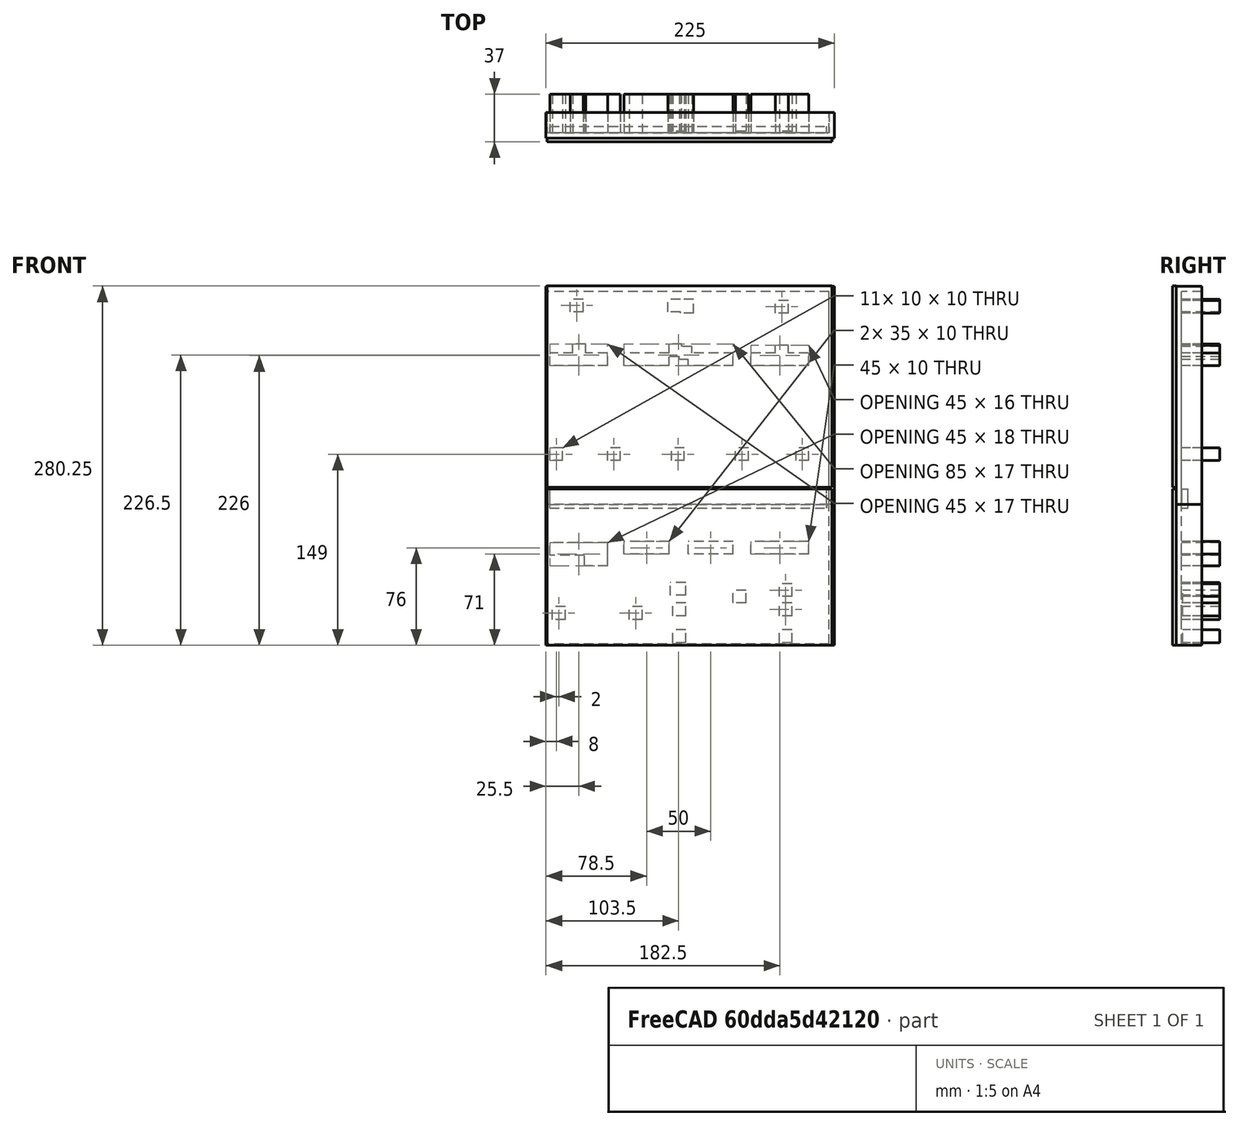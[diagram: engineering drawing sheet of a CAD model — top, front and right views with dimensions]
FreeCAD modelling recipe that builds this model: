
FCSTD DOCUMENT  (FreeCAD 0.19R24291 (Git))
Label: estructuraBase
License: All rights reserved
LicenseURL: http://en.wikipedia.org/wiki/All_rights_reserved
objects: Part::Box×154, Part::MultiFuse×11, Part::Cut×7, Part::Feature×2
note: 174 computed .brp shape members not serialized (recipe doc carries the construction recipe); baked Part::Feature solids carry a one-line shape summary decoded from their .brp

FEATURE [Part::Box] Box  label="Cubo"
  AttacherType = Attacher::AttachEngine3D
  Height = 275
  Length = 220
  Placement = pos=(-171,-24,-147) rot=(0,0,1;0rad)
  Width = 4
FEATURE [Part::Box] Box001  label="Cubo001"
  AttacherType = Attacher::AttachEngine3D
  Height = 10
  Length = 35
  Placement = pos=(-96,-54,70) rot=(0,0,1;0rad)
  Width = 30
FEATURE [Part::Box] Box002  label="Cubo002"
  AttacherType = Attacher::AttachEngine3D
  Height = 10
  Length = 10
  Placement = pos=(-142,-54,-110) rot=(0,0,1;0rad)
  Width = 30
FEATURE [Part::Box] Box004  label="Cubo004"
  AttacherType = Attacher::AttachEngine3D
  Height = 10
  Length = 10
  Placement = pos=(-142,-54,-125) rot=(0,0,1;0rad)
  Width = 30
FEATURE [Part::Box] Box005  label="Cubo005"
  AttacherType = Attacher::AttachEngine3D
  Height = 10
  Length = 10
  Placement = pos=(-106,-54,-115) rot=(0,0,1;0rad)
  Width = 28.9
FEATURE [Part::Box] Box006  label="Cubo006"
  AttacherType = Attacher::AttachEngine3D
  Height = 10
  Length = 10
  Placement = pos=(-142,-54,-146) rot=(0,0,1;0rad)
  Width = 28.9
FEATURE [Part::Box] Box007  label="Cubo007"
  AttacherType = Attacher::AttachEngine3D
  Height = 10
  Length = 10
  Placement = pos=(-59,-54,-146) rot=(0,0,1;0rad)
  Width = 28.9
FEATURE [Part::Box] Box008  label="Cubo008"
  AttacherType = Attacher::AttachEngine3D
  Height = 10
  Length = 10
  Placement = pos=(-59,-54,-125) rot=(0,0,1;0rad)
  Width = 28.9
FEATURE [Part::Box] Box009  label="Cubo009"
  AttacherType = Attacher::AttachEngine3D
  Height = 10
  Length = 12
  Placement = pos=(-59,-54,-109) rot=(0,0,1;0rad)
  Width = 30
FEATURE [Part::Box] Box010  label="Cubo010"
  AttacherType = Attacher::AttachEngine3D
  Height = 10
  Length = 45
  Placement = pos=(-155,-54,70) rot=(0,0,1;0rad)
  Width = 30
FEATURE [Part::Box] Box011  label="Cubo011"
  AttacherType = Attacher::AttachEngine3D
  Height = 10
  Length = 35
  Placement = pos=(-46,-54,70) rot=(0,0,1;0rad)
  Width = 30
FEATURE [Part::Box] Box012  label="Cubo012"
  AttacherType = Attacher::AttachEngine3D
  Height = 10
  Length = 45
  Placement = pos=(2,-54,70) rot=(0,0,1;0rad)
  Width = 30
FEATURE [Part::Box] Box013  label="Cubo013"
  AttacherType = Attacher::AttachEngine3D
  Height = 10
  Length = 35
  Placement = pos=(-96,-54,-77) rot=(0,0,1;0rad)
  Width = 30
FEATURE [Part::Box] Box014  label="Cubo014"
  AttacherType = Attacher::AttachEngine3D
  Height = 10
  Length = 45
  Placement = pos=(-155,-54,-77) rot=(0,0,1;0rad)
  Width = 30
FEATURE [Part::Box] Box015  label="Cubo015"
  AttacherType = Attacher::AttachEngine3D
  Height = 10
  Length = 35
  Placement = pos=(-46,-54,-77) rot=(0,0,1;0rad)
  Width = 30
FEATURE [Part::Box] Box016  label="Cubo016"
  AttacherType = Attacher::AttachEngine3D
  Height = 10
  Length = 45
  Placement = pos=(2,-54,-78) rot=(0,0,1;0rad)
  Width = 30
FEATURE [Part::Box] Box017  label="Cubo017"
  AttacherType = Attacher::AttachEngine3D
  Height = 10
  Length = 10
  Placement = pos=(-25,-54,-128) rot=(0,0,1;0rad)
  Width = 30
FEATURE [Part::Box] Box018  label="Cubo018"
  AttacherType = Attacher::AttachEngine3D
  Height = 10
  Length = 10
  Placement = pos=(35,-54,-128) rot=(0,0,1;0rad)
  Width = 30
FEATURE [Part::Box] Box019  label="Cubo019"
  AttacherType = Attacher::AttachEngine3D
  Height = 10
  Length = 18
  Placement = pos=(2,-54,-86) rot=(0,0,1;0rad)
  Width = 30
FEATURE [Part::Box] Box020  label="Cubo020"
  AttacherType = Attacher::AttachEngine3D
  Height = 10
  Length = 10
  Placement = pos=(-56,-54,77) rot=(0,0,1;0rad)
  Width = 30
FEATURE [Part::Box] Box021  label="Cubo021"
  AttacherType = Attacher::AttachEngine3D
  Height = 10
  Length = 10
  Placement = pos=(21,-54,112) rot=(0,0,1;0rad)
  Width = 30
FEATURE [Part::Box] Box022  label="Cubo022"
  AttacherType = Attacher::AttachEngine3D
  Height = 10
  Length = 10
  Placement = pos=(-55,-54,112) rot=(0,0,1;0rad)
  Width = 30
FEATURE [Part::Box] Box023  label="Cubo023"
  AttacherType = Attacher::AttachEngine3D
  Height = 10
  Length = 10
  Placement = pos=(19,-54,77) rot=(0,0,1;0rad)
  Width = 30
FEATURE [Part::Box] Box024  label="Cubo024"
  AttacherType = Attacher::AttachEngine3D
  Height = 11
  Length = 10
  Placement = pos=(-65,-54,111) rot=(0,0,1;0rad)
  Width = 30
FEATURE [Part::Box] Box025  label="Cubo025"
  AttacherType = Attacher::AttachEngine3D
  Height = 10
  Length = 10
  Placement = pos=(-139,-54,111) rot=(0,0,1;0rad)
  Width = 30
FEATURE [Part::Box] Box026  label="Cubo026"
  AttacherType = Attacher::AttachEngine3D
  Height = 10
  Length = 10
  Placement = pos=(-139,-54,76) rot=(0,0,1;0rad)
  Width = 30
FEATURE [Part::Box] Box027  label="Cubo027"
  AttacherType = Attacher::AttachEngine3D
  Height = 10
  Length = 10
  Placement = pos=(-64,-54,75) rot=(0,0,1;0rad)
  Width = 30
FEATURE [Part::Box] Box028  label="Cubo028"
  AttacherType = Attacher::AttachEngine3D
  Height = 10
  Length = 10
  Placement = pos=(-155,-54,-4) rot=(0,0,1;0rad)
  Width = 30
FEATURE [Part::Box] Box029  label="Cubo029"
  AttacherType = Attacher::AttachEngine3D
  Height = 10
  Length = 10
  Placement = pos=(37,-54,-4) rot=(0,0,1;0rad)
  Width = 30
FEATURE [Part::Box] Box030  label="Cubo030"
  AttacherType = Attacher::AttachEngine3D
  Height = 10
  Length = 10
  Placement = pos=(-108,-54,-4) rot=(0,0,1;0rad)
  Width = 30
FEATURE [Part::Box] Box031  label="Cubo031"
  AttacherType = Attacher::AttachEngine3D
  Height = 10
  Length = 10
  Placement = pos=(-58,-54,-4) rot=(0,0,1;0rad)
  Width = 30
FEATURE [Part::Box] Box032  label="Cubo032"
  AttacherType = Attacher::AttachEngine3D
  Height = 10
  Length = 10
  Placement = pos=(-8,-54,-4) rot=(0,0,1;0rad)
  Width = 30
FEATURE [Part::Box] Box033  label="Cubo033"
  AttacherType = Attacher::AttachEngine3D
  Height = 275
  Length = 1
  Placement = pos=(-49,40,-147) rot=(0,0,1;3.14159rad)
  Width = 20
FEATURE [Part::Box] Box034  label="Cubo034"
  AttacherType = Attacher::AttachEngine3D
  Height = 275
  Length = 4
  Placement = pos=(175,40,-147) rot=(0,0,1;3.14159rad)
  Width = 20
FEATURE [Part::Box] Box035  label="Cubo035"
  AttacherType = Attacher::AttachEngine3D
  Height = 4
  Length = 225
  Placement = pos=(175,40,128) rot=(0,0,1;3.14159rad)
  Width = 20
FEATURE [Part::Box] Box036  label="Cubo036"
  AttacherType = Attacher::AttachEngine3D
  Height = 1
  Length = 225
  Placement = pos=(175,40,-148) rot=(0,0,1;3.14159rad)
  Width = 20
FEATURE [Part::Box] Box037  label="Cubo037"
  AttacherType = Attacher::AttachEngine3D
  Height = 200
  Length = 300
  Placement = pos=(-111,11,-38) rot=(0,0,1;0rad)
  Width = 50
FEATURE [Part::Feature] Cut002_solid  label="Parte1 (Solid)001"
  shape: bbox 222 x 37 x 122 mm, 103 faces (baked)
FEATURE [Part::Box] Box039  label="Cubo039"
  AttacherType = Attacher::AttachEngine3D
  Height = 157
  Length = 222
  Placement = pos=(-49,17,-24.75) rot=(0,0,1;0rad)
  Width = 3
FEATURE [Part::Box] Box041  label="Cubo041"
  AttacherType = Attacher::AttachEngine3D
  Height = 107
  Length = 222
  Placement = pos=(-49,17,-148) rot=(0,0,1;0rad)
  Width = 3
FEATURE [Part::Box] Box042  label="Cubo042"
  AttacherType = Attacher::AttachEngine3D
  Height = 15
  Length = 2
  Placement = pos=(-49,17,-41) rot=(0,0,1;0rad)
  Width = 3
FEATURE [Part::Box] Box043  label="Cubo043"
  AttacherType = Attacher::AttachEngine3D
  Height = 15
  Length = 4
  Placement = pos=(169,17,-41) rot=(0,0,1;0rad)
  Width = 3
FEATURE [Part::Box] Box044  label="Cubo044"
  AttacherType = Attacher::AttachEngine3D
  Height = 12
  Length = 222
  Placement = pos=(-49,24,-38) rot=(0,0,1;0rad)
  Width = 0.25
FEATURE [Part::MultiFuse] Fusion
  Placement = pos=(0,0,0) rot=(0,0,1;3.14159rad)
  Shapes = -> [Box,Box001,Box002,Box004,Box005,Box006,Box007,Box009,Box008,Box010,Box012,Box011,Box013,Box014,Box015,Box016,Box018,Box017,Box019,Box020,Box021,Box022,Box023,Box032,Box031,Box030,Box028,Box027,Box024,Box025,Box026,Box029]
FEATURE [Part::MultiFuse] Fusion010  label="CompletoConParedes"
  Shapes = -> [Fusion,Box033,Box034,Box035,Box036]
FEATURE [Part::Box] Box045  label="Cubo045"
  AttacherType = Attacher::AttachEngine3D
  Height = 275
  Length = 220
  Placement = pos=(-171,-24,-147) rot=(0,0,1;0rad)
  Width = 4
FEATURE [Part::Box] Box046  label="Cubo046"
  AttacherType = Attacher::AttachEngine3D
  Height = 10
  Length = 35
  Placement = pos=(-96,-54,70) rot=(0,0,1;0rad)
  Width = 30
FEATURE [Part::Box] Box047  label="Cubo047"
  AttacherType = Attacher::AttachEngine3D
  Height = 10
  Length = 10
  Placement = pos=(-142,-54,-110) rot=(0,0,1;0rad)
  Width = 30
FEATURE [Part::Box] Box048  label="Cubo048"
  AttacherType = Attacher::AttachEngine3D
  Height = 10
  Length = 10
  Placement = pos=(-142,-54,-125) rot=(0,0,1;0rad)
  Width = 30
FEATURE [Part::Box] Box049  label="Cubo049"
  AttacherType = Attacher::AttachEngine3D
  Height = 10
  Length = 10
  Placement = pos=(-106,-54,-115) rot=(0,0,1;0rad)
  Width = 28.9
FEATURE [Part::Box] Box050  label="Cubo050"
  AttacherType = Attacher::AttachEngine3D
  Height = 10
  Length = 10
  Placement = pos=(-142,-54,-146) rot=(0,0,1;0rad)
  Width = 28.9
FEATURE [Part::Box] Box051  label="Cubo051"
  AttacherType = Attacher::AttachEngine3D
  Height = 10
  Length = 10
  Placement = pos=(-59,-54,-146) rot=(0,0,1;0rad)
  Width = 28.9
FEATURE [Part::Box] Box052  label="Cubo052"
  AttacherType = Attacher::AttachEngine3D
  Height = 10
  Length = 10
  Placement = pos=(-59,-54,-125) rot=(0,0,1;0rad)
  Width = 28.9
FEATURE [Part::Box] Box053  label="Cubo053"
  AttacherType = Attacher::AttachEngine3D
  Height = 10
  Length = 12
  Placement = pos=(-59,-54,-109) rot=(0,0,1;0rad)
  Width = 30
FEATURE [Part::Box] Box054  label="Cubo054"
  AttacherType = Attacher::AttachEngine3D
  Height = 10
  Length = 45
  Placement = pos=(-155,-54,70) rot=(0,0,1;0rad)
  Width = 30
FEATURE [Part::Box] Box055  label="Cubo055"
  AttacherType = Attacher::AttachEngine3D
  Height = 10
  Length = 35
  Placement = pos=(-46,-54,70) rot=(0,0,1;0rad)
  Width = 30
FEATURE [Part::Box] Box056  label="Cubo056"
  AttacherType = Attacher::AttachEngine3D
  Height = 10
  Length = 45
  Placement = pos=(2,-54,70) rot=(0,0,1;0rad)
  Width = 30
FEATURE [Part::Box] Box057  label="Cubo057"
  AttacherType = Attacher::AttachEngine3D
  Height = 10
  Length = 35
  Placement = pos=(-96,-54,-77) rot=(0,0,1;0rad)
  Width = 30
FEATURE [Part::Box] Box058  label="Cubo058"
  AttacherType = Attacher::AttachEngine3D
  Height = 10
  Length = 45
  Placement = pos=(-155,-54,-77) rot=(0,0,1;0rad)
  Width = 30
FEATURE [Part::Box] Box059  label="Cubo059"
  AttacherType = Attacher::AttachEngine3D
  Height = 10
  Length = 35
  Placement = pos=(-46,-54,-77) rot=(0,0,1;0rad)
  Width = 30
FEATURE [Part::Box] Box060  label="Cubo060"
  AttacherType = Attacher::AttachEngine3D
  Height = 10
  Length = 45
  Placement = pos=(2,-54,-78) rot=(0,0,1;0rad)
  Width = 30
FEATURE [Part::Box] Box061  label="Cubo061"
  AttacherType = Attacher::AttachEngine3D
  Height = 10
  Length = 10
  Placement = pos=(-25,-54,-128) rot=(0,0,1;0rad)
  Width = 30
FEATURE [Part::Box] Box062  label="Cubo062"
  AttacherType = Attacher::AttachEngine3D
  Height = 10
  Length = 10
  Placement = pos=(35,-54,-128) rot=(0,0,1;0rad)
  Width = 30
FEATURE [Part::Box] Box063  label="Cubo063"
  AttacherType = Attacher::AttachEngine3D
  Height = 10
  Length = 18
  Placement = pos=(2,-54,-86) rot=(0,0,1;0rad)
  Width = 30
FEATURE [Part::Box] Box064  label="Cubo064"
  AttacherType = Attacher::AttachEngine3D
  Height = 10
  Length = 10
  Placement = pos=(-56,-54,77) rot=(0,0,1;0rad)
  Width = 30
FEATURE [Part::Box] Box065  label="Cubo065"
  AttacherType = Attacher::AttachEngine3D
  Height = 10
  Length = 10
  Placement = pos=(21,-54,112) rot=(0,0,1;0rad)
  Width = 30
FEATURE [Part::Box] Box066  label="Cubo066"
  AttacherType = Attacher::AttachEngine3D
  Height = 10
  Length = 10
  Placement = pos=(-55,-54,112) rot=(0,0,1;0rad)
  Width = 30
FEATURE [Part::Box] Box067  label="Cubo067"
  AttacherType = Attacher::AttachEngine3D
  Height = 10
  Length = 10
  Placement = pos=(19,-54,77) rot=(0,0,1;0rad)
  Width = 30
FEATURE [Part::Box] Box068  label="Cubo068"
  AttacherType = Attacher::AttachEngine3D
  Height = 11
  Length = 10
  Placement = pos=(-65,-54,111) rot=(0,0,1;0rad)
  Width = 30
FEATURE [Part::Box] Box069  label="Cubo069"
  AttacherType = Attacher::AttachEngine3D
  Height = 10
  Length = 10
  Placement = pos=(-139,-54,111) rot=(0,0,1;0rad)
  Width = 30
FEATURE [Part::Box] Box070  label="Cubo070"
  AttacherType = Attacher::AttachEngine3D
  Height = 10
  Length = 10
  Placement = pos=(-139,-54,76) rot=(0,0,1;0rad)
  Width = 30
FEATURE [Part::Box] Box071  label="Cubo071"
  AttacherType = Attacher::AttachEngine3D
  Height = 10
  Length = 10
  Placement = pos=(-64,-54,75) rot=(0,0,1;0rad)
  Width = 30
FEATURE [Part::Box] Box072  label="Cubo072"
  AttacherType = Attacher::AttachEngine3D
  Height = 10
  Length = 10
  Placement = pos=(-155,-54,-4) rot=(0,0,1;0rad)
  Width = 30
FEATURE [Part::Box] Box073  label="Cubo073"
  AttacherType = Attacher::AttachEngine3D
  Height = 10
  Length = 10
  Placement = pos=(37,-54,-4) rot=(0,0,1;0rad)
  Width = 30
FEATURE [Part::Box] Box074  label="Cubo074"
  AttacherType = Attacher::AttachEngine3D
  Height = 10
  Length = 10
  Placement = pos=(-108,-54,-4) rot=(0,0,1;0rad)
  Width = 30
FEATURE [Part::Box] Box075  label="Cubo075"
  AttacherType = Attacher::AttachEngine3D
  Height = 10
  Length = 10
  Placement = pos=(-58,-54,-4) rot=(0,0,1;0rad)
  Width = 30
FEATURE [Part::Box] Box076  label="Cubo076"
  AttacherType = Attacher::AttachEngine3D
  Height = 10
  Length = 10
  Placement = pos=(-8,-54,-4) rot=(0,0,1;0rad)
  Width = 30
FEATURE [Part::Box] Box077  label="Cubo077"
  AttacherType = Attacher::AttachEngine3D
  Height = 275
  Length = 1
  Placement = pos=(-49,40,-147) rot=(0,0,1;3.14159rad)
  Width = 20
FEATURE [Part::Box] Box078  label="Cubo078"
  AttacherType = Attacher::AttachEngine3D
  Height = 275
  Length = 4
  Placement = pos=(175,40,-147) rot=(0,0,1;3.14159rad)
  Width = 20
FEATURE [Part::Box] Box079  label="Cubo079"
  AttacherType = Attacher::AttachEngine3D
  Height = 4
  Length = 225
  Placement = pos=(175,40,128) rot=(0,0,1;3.14159rad)
  Width = 20
FEATURE [Part::Box] Box080  label="Cubo080"
  AttacherType = Attacher::AttachEngine3D
  Height = 1
  Length = 225
  Placement = pos=(175,40,-148) rot=(0,0,1;3.14159rad)
  Width = 20
FEATURE [Part::MultiFuse] Fusion011
  Placement = pos=(0,0,0) rot=(0,0,1;3.14159rad)
  Shapes = -> [Box045,Box046,Box047,Box048,Box049,Box050,Box051,Box053,Box052,Box054,Box056,Box055,Box057,Box058,Box059,Box060,Box062,Box061,Box063,Box064,Box065,Box066,Box067,Box076,Box075,Box074,Box072,Box071,Box068,Box069,Box070,Box073]
FEATURE [Part::MultiFuse] Fusion012  label="CompletoConParedes001"
  Shapes = -> [Fusion011,Box077,Box078,Box079,Box080]
FEATURE [Part::Cut] Cut
  Base = -> Fusion012
  Tool = -> Box037
FEATURE [Part::Box] Box081  label="Cubo081"
  AttacherType = Attacher::AttachEngine3D
  Height = 200
  Length = 300
  Placement = pos=(-111,11,-38) rot=(0,0,1;0rad)
  Width = 50
FEATURE [Part::Box] Box082  label="Cubo082"
  AttacherType = Attacher::AttachEngine3D
  Height = 10
  Length = 10
  Placement = pos=(35,-54,-128) rot=(0,0,1;0rad)
  Width = 30
FEATURE [Part::Box] Box083  label="Cubo083"
  AttacherType = Attacher::AttachEngine3D
  Height = 10
  Length = 18
  Placement = pos=(2,-54,-86) rot=(0,0,1;0rad)
  Width = 30
FEATURE [Part::Box] Box084  label="Cubo084"
  AttacherType = Attacher::AttachEngine3D
  Height = 10
  Length = 10
  Placement = pos=(-56,-54,77) rot=(0,0,1;0rad)
  Width = 30
FEATURE [Part::Box] Box085  label="Cubo085"
  AttacherType = Attacher::AttachEngine3D
  Height = 10
  Length = 10
  Placement = pos=(21,-54,112) rot=(0,0,1;0rad)
  Width = 30
FEATURE [Part::Box] Box086  label="Cubo086"
  AttacherType = Attacher::AttachEngine3D
  Height = 10
  Length = 10
  Placement = pos=(-55,-54,112) rot=(0,0,1;0rad)
  Width = 30
FEATURE [Part::Box] Box087  label="Cubo087"
  AttacherType = Attacher::AttachEngine3D
  Height = 10
  Length = 10
  Placement = pos=(19,-54,77) rot=(0,0,1;0rad)
  Width = 30
FEATURE [Part::Box] Box088  label="Cubo088"
  AttacherType = Attacher::AttachEngine3D
  Height = 11
  Length = 10
  Placement = pos=(-65,-54,111) rot=(0,0,1;0rad)
  Width = 30
FEATURE [Part::Box] Box089  label="Cubo089"
  AttacherType = Attacher::AttachEngine3D
  Height = 10
  Length = 10
  Placement = pos=(-139,-54,111) rot=(0,0,1;0rad)
  Width = 30
FEATURE [Part::Box] Box090  label="Cubo090"
  AttacherType = Attacher::AttachEngine3D
  Height = 10
  Length = 10
  Placement = pos=(-139,-54,76) rot=(0,0,1;0rad)
  Width = 30
FEATURE [Part::Box] Box091  label="Cubo091"
  AttacherType = Attacher::AttachEngine3D
  Height = 10
  Length = 10
  Placement = pos=(-142,-54,-146) rot=(0,0,1;0rad)
  Width = 28.9
FEATURE [Part::Box] Box092  label="Cubo092"
  AttacherType = Attacher::AttachEngine3D
  Height = 10
  Length = 10
  Placement = pos=(-59,-54,-146) rot=(0,0,1;0rad)
  Width = 28.9
FEATURE [Part::Box] Box093  label="Cubo093"
  AttacherType = Attacher::AttachEngine3D
  Height = 10
  Length = 10
  Placement = pos=(-59,-54,-125) rot=(0,0,1;0rad)
  Width = 28.9
FEATURE [Part::Box] Box094  label="Cubo094"
  AttacherType = Attacher::AttachEngine3D
  Height = 10
  Length = 12
  Placement = pos=(-59,-54,-109) rot=(0,0,1;0rad)
  Width = 30
FEATURE [Part::Box] Box095  label="Cubo095"
  AttacherType = Attacher::AttachEngine3D
  Height = 10
  Length = 45
  Placement = pos=(-155,-54,70) rot=(0,0,1;0rad)
  Width = 30
FEATURE [Part::Box] Box096  label="Cubo096"
  AttacherType = Attacher::AttachEngine3D
  Height = 10
  Length = 35
  Placement = pos=(-46,-54,70) rot=(0,0,1;0rad)
  Width = 30
FEATURE [Part::Box] Box097  label="Cubo097"
  AttacherType = Attacher::AttachEngine3D
  Height = 10
  Length = 45
  Placement = pos=(2,-54,70) rot=(0,0,1;0rad)
  Width = 30
FEATURE [Part::Box] Box098  label="Cubo098"
  AttacherType = Attacher::AttachEngine3D
  Height = 10
  Length = 35
  Placement = pos=(-96,-54,-77) rot=(0,0,1;0rad)
  Width = 30
FEATURE [Part::Box] Box099  label="Cubo099"
  AttacherType = Attacher::AttachEngine3D
  Height = 10
  Length = 45
  Placement = pos=(-155,-54,-77) rot=(0,0,1;0rad)
  Width = 30
FEATURE [Part::Box] Box100  label="Cubo100"
  AttacherType = Attacher::AttachEngine3D
  Height = 10
  Length = 35
  Placement = pos=(-46,-54,-77) rot=(0,0,1;0rad)
  Width = 30
FEATURE [Part::Box] Box101  label="Cubo101"
  AttacherType = Attacher::AttachEngine3D
  Height = 10
  Length = 45
  Placement = pos=(2,-54,-78) rot=(0,0,1;0rad)
  Width = 30
FEATURE [Part::Box] Box102  label="Cubo102"
  AttacherType = Attacher::AttachEngine3D
  Height = 10
  Length = 10
  Placement = pos=(-25,-54,-128) rot=(0,0,1;0rad)
  Width = 30
FEATURE [Part::Box] Box103  label="Cubo103"
  AttacherType = Attacher::AttachEngine3D
  Height = 10
  Length = 35
  Placement = pos=(-96,-54,70) rot=(0,0,1;0rad)
  Width = 30
FEATURE [Part::Box] Box104  label="Cubo104"
  AttacherType = Attacher::AttachEngine3D
  Height = 10
  Length = 10
  Placement = pos=(-142,-54,-110) rot=(0,0,1;0rad)
  Width = 30
FEATURE [Part::Box] Box105  label="Cubo105"
  AttacherType = Attacher::AttachEngine3D
  Height = 10
  Length = 10
  Placement = pos=(-142,-54,-125) rot=(0,0,1;0rad)
  Width = 30
FEATURE [Part::Box] Box106  label="Cubo106"
  AttacherType = Attacher::AttachEngine3D
  Height = 10
  Length = 10
  Placement = pos=(-106,-54,-115) rot=(0,0,1;0rad)
  Width = 28.9
FEATURE [Part::Box] Box107  label="Cubo107"
  AttacherType = Attacher::AttachEngine3D
  Height = 275
  Length = 220
  Placement = pos=(-171,-24,-147) rot=(0,0,1;0rad)
  Width = 4
FEATURE [Part::Box] Box108  label="Cubo108"
  AttacherType = Attacher::AttachEngine3D
  Height = 10
  Length = 10
  Placement = pos=(-64,-54,75) rot=(0,0,1;0rad)
  Width = 30
FEATURE [Part::Box] Box109  label="Cubo109"
  AttacherType = Attacher::AttachEngine3D
  Height = 10
  Length = 10
  Placement = pos=(-155,-54,-4) rot=(0,0,1;0rad)
  Width = 30
FEATURE [Part::Box] Box110  label="Cubo110"
  AttacherType = Attacher::AttachEngine3D
  Height = 10
  Length = 10
  Placement = pos=(37,-54,-4) rot=(0,0,1;0rad)
  Width = 30
FEATURE [Part::Box] Box111  label="Cubo111"
  AttacherType = Attacher::AttachEngine3D
  Height = 10
  Length = 10
  Placement = pos=(-108,-54,-4) rot=(0,0,1;0rad)
  Width = 30
FEATURE [Part::Box] Box112  label="Cubo112"
  AttacherType = Attacher::AttachEngine3D
  Height = 10
  Length = 10
  Placement = pos=(-58,-54,-4) rot=(0,0,1;0rad)
  Width = 30
FEATURE [Part::Box] Box113  label="Cubo113"
  AttacherType = Attacher::AttachEngine3D
  Height = 10
  Length = 10
  Placement = pos=(-8,-54,-4) rot=(0,0,1;0rad)
  Width = 30
FEATURE [Part::Box] Box114  label="Cubo114"
  AttacherType = Attacher::AttachEngine3D
  Height = 275
  Length = 1
  Placement = pos=(-49,40,-147) rot=(0,0,1;3.14159rad)
  Width = 20
FEATURE [Part::Box] Box115  label="Cubo115"
  AttacherType = Attacher::AttachEngine3D
  Height = 275
  Length = 4
  Placement = pos=(175,40,-147) rot=(0,0,1;3.14159rad)
  Width = 20
FEATURE [Part::Box] Box116  label="Cubo116"
  AttacherType = Attacher::AttachEngine3D
  Height = 4
  Length = 225
  Placement = pos=(175,40,128) rot=(0,0,1;3.14159rad)
  Width = 20
FEATURE [Part::Box] Box117  label="Cubo117"
  AttacherType = Attacher::AttachEngine3D
  Height = 1
  Length = 225
  Placement = pos=(175,40,-148) rot=(0,0,1;3.14159rad)
  Width = 20
FEATURE [Part::MultiFuse] Fusion013
  Placement = pos=(0,0,0) rot=(0,0,1;3.14159rad)
  Shapes = -> [Box107,Box103,Box104,Box105,Box106,Box091,Box092,Box094,Box093,Box095,Box097,Box096,Box098,Box099,Box100,Box101,Box082,Box102,Box083,Box084,Box085,Box086,Box087,Box113,Box112,Box111,Box109,Box108,Box088,Box089,Box090,Box110]
FEATURE [Part::MultiFuse] Fusion014  label="CompletoConParedes002"
  Shapes = -> [Fusion013,Box114,Box115,Box116,Box117]
FEATURE [Part::Cut] Cut004
  Base = -> Fusion014
  Tool = -> Box081
FEATURE [Part::Box] Box118  label="Cubo118"
  AttacherType = Attacher::AttachEngine3D
  Height = 275
  Length = 220
  Placement = pos=(-171,-24,-147) rot=(0,0,1;0rad)
  Width = 4
FEATURE [Part::Box] Box119  label="Cubo119"
  AttacherType = Attacher::AttachEngine3D
  Height = 10
  Length = 35
  Placement = pos=(-96,-54,70) rot=(0,0,1;0rad)
  Width = 30
FEATURE [Part::Box] Box120  label="Cubo120"
  AttacherType = Attacher::AttachEngine3D
  Height = 10
  Length = 10
  Placement = pos=(-142,-54,-110) rot=(0,0,1;0rad)
  Width = 30
FEATURE [Part::Box] Box121  label="Cubo121"
  AttacherType = Attacher::AttachEngine3D
  Height = 10
  Length = 10
  Placement = pos=(-142,-54,-125) rot=(0,0,1;0rad)
  Width = 30
FEATURE [Part::Box] Box122  label="Cubo122"
  AttacherType = Attacher::AttachEngine3D
  Height = 10
  Length = 10
  Placement = pos=(-106,-54,-115) rot=(0,0,1;0rad)
  Width = 28.9
FEATURE [Part::Box] Box123  label="Cubo123"
  AttacherType = Attacher::AttachEngine3D
  Height = 10
  Length = 10
  Placement = pos=(-142,-54,-146) rot=(0,0,1;0rad)
  Width = 28.9
FEATURE [Part::Box] Box124  label="Cubo124"
  AttacherType = Attacher::AttachEngine3D
  Height = 10
  Length = 10
  Placement = pos=(-59,-54,-146) rot=(0,0,1;0rad)
  Width = 28.9
FEATURE [Part::Box] Box125  label="Cubo125"
  AttacherType = Attacher::AttachEngine3D
  Height = 10
  Length = 10
  Placement = pos=(-59,-54,-125) rot=(0,0,1;0rad)
  Width = 28.9
FEATURE [Part::Box] Box126  label="Cubo126"
  AttacherType = Attacher::AttachEngine3D
  Height = 10
  Length = 12
  Placement = pos=(-59,-54,-109) rot=(0,0,1;0rad)
  Width = 30
FEATURE [Part::Box] Box127  label="Cubo127"
  AttacherType = Attacher::AttachEngine3D
  Height = 10
  Length = 45
  Placement = pos=(-155,-54,70) rot=(0,0,1;0rad)
  Width = 30
FEATURE [Part::Box] Box128  label="Cubo128"
  AttacherType = Attacher::AttachEngine3D
  Height = 10
  Length = 35
  Placement = pos=(-46,-54,70) rot=(0,0,1;0rad)
  Width = 30
FEATURE [Part::Box] Box129  label="Cubo129"
  AttacherType = Attacher::AttachEngine3D
  Height = 10
  Length = 45
  Placement = pos=(2,-54,70) rot=(0,0,1;0rad)
  Width = 30
FEATURE [Part::Box] Box130  label="Cubo130"
  AttacherType = Attacher::AttachEngine3D
  Height = 10
  Length = 35
  Placement = pos=(-96,-54,-77) rot=(0,0,1;0rad)
  Width = 30
FEATURE [Part::Box] Box131  label="Cubo131"
  AttacherType = Attacher::AttachEngine3D
  Height = 10
  Length = 45
  Placement = pos=(-155,-54,-77) rot=(0,0,1;0rad)
  Width = 30
FEATURE [Part::Box] Box132  label="Cubo132"
  AttacherType = Attacher::AttachEngine3D
  Height = 10
  Length = 35
  Placement = pos=(-46,-54,-77) rot=(0,0,1;0rad)
  Width = 30
FEATURE [Part::Box] Box133  label="Cubo133"
  AttacherType = Attacher::AttachEngine3D
  Height = 10
  Length = 45
  Placement = pos=(2,-54,-78) rot=(0,0,1;0rad)
  Width = 30
FEATURE [Part::Box] Box134  label="Cubo134"
  AttacherType = Attacher::AttachEngine3D
  Height = 10
  Length = 10
  Placement = pos=(-25,-54,-128) rot=(0,0,1;0rad)
  Width = 30
FEATURE [Part::Box] Box135  label="Cubo135"
  AttacherType = Attacher::AttachEngine3D
  Height = 10
  Length = 10
  Placement = pos=(35,-54,-128) rot=(0,0,1;0rad)
  Width = 30
FEATURE [Part::Box] Box136  label="Cubo136"
  AttacherType = Attacher::AttachEngine3D
  Height = 10
  Length = 18
  Placement = pos=(2,-54,-86) rot=(0,0,1;0rad)
  Width = 30
FEATURE [Part::Box] Box137  label="Cubo137"
  AttacherType = Attacher::AttachEngine3D
  Height = 10
  Length = 10
  Placement = pos=(-56,-54,77) rot=(0,0,1;0rad)
  Width = 30
FEATURE [Part::Box] Box138  label="Cubo138"
  AttacherType = Attacher::AttachEngine3D
  Height = 10
  Length = 10
  Placement = pos=(21,-54,112) rot=(0,0,1;0rad)
  Width = 30
FEATURE [Part::Box] Box139  label="Cubo139"
  AttacherType = Attacher::AttachEngine3D
  Height = 10
  Length = 10
  Placement = pos=(-55,-54,112) rot=(0,0,1;0rad)
  Width = 30
FEATURE [Part::Box] Box140  label="Cubo140"
  AttacherType = Attacher::AttachEngine3D
  Height = 10
  Length = 10
  Placement = pos=(19,-54,77) rot=(0,0,1;0rad)
  Width = 30
FEATURE [Part::Box] Box141  label="Cubo141"
  AttacherType = Attacher::AttachEngine3D
  Height = 11
  Length = 10
  Placement = pos=(-65,-54,111) rot=(0,0,1;0rad)
  Width = 30
FEATURE [Part::Box] Box142  label="Cubo142"
  AttacherType = Attacher::AttachEngine3D
  Height = 10
  Length = 10
  Placement = pos=(-139,-54,111) rot=(0,0,1;0rad)
  Width = 30
FEATURE [Part::Box] Box143  label="Cubo143"
  AttacherType = Attacher::AttachEngine3D
  Height = 10
  Length = 10
  Placement = pos=(-139,-54,76) rot=(0,0,1;0rad)
  Width = 30
FEATURE [Part::Box] Box144  label="Cubo144"
  AttacherType = Attacher::AttachEngine3D
  Height = 10
  Length = 10
  Placement = pos=(-64,-54,75) rot=(0,0,1;0rad)
  Width = 30
FEATURE [Part::Box] Box145  label="Cubo145"
  AttacherType = Attacher::AttachEngine3D
  Height = 10
  Length = 10
  Placement = pos=(-155,-54,-4) rot=(0,0,1;0rad)
  Width = 30
FEATURE [Part::Box] Box146  label="Cubo146"
  AttacherType = Attacher::AttachEngine3D
  Height = 10
  Length = 10
  Placement = pos=(37,-54,-4) rot=(0,0,1;0rad)
  Width = 30
FEATURE [Part::Box] Box147  label="Cubo147"
  AttacherType = Attacher::AttachEngine3D
  Height = 10
  Length = 10
  Placement = pos=(-108,-54,-4) rot=(0,0,1;0rad)
  Width = 30
FEATURE [Part::Box] Box148  label="Cubo148"
  AttacherType = Attacher::AttachEngine3D
  Height = 10
  Length = 10
  Placement = pos=(-58,-54,-4) rot=(0,0,1;0rad)
  Width = 30
FEATURE [Part::Box] Box149  label="Cubo149"
  AttacherType = Attacher::AttachEngine3D
  Height = 10
  Length = 10
  Placement = pos=(-8,-54,-4) rot=(0,0,1;0rad)
  Width = 30
FEATURE [Part::Box] Box150  label="Cubo150"
  AttacherType = Attacher::AttachEngine3D
  Height = 275
  Length = 1
  Placement = pos=(-49,40,-147) rot=(0,0,1;3.14159rad)
  Width = 20
FEATURE [Part::Box] Box151  label="Cubo151"
  AttacherType = Attacher::AttachEngine3D
  Height = 275
  Length = 4
  Placement = pos=(175,40,-147) rot=(0,0,1;3.14159rad)
  Width = 20
FEATURE [Part::Box] Box152  label="Cubo152"
  AttacherType = Attacher::AttachEngine3D
  Height = 4
  Length = 225
  Placement = pos=(175,40,128) rot=(0,0,1;3.14159rad)
  Width = 20
FEATURE [Part::Box] Box153  label="Cubo153"
  AttacherType = Attacher::AttachEngine3D
  Height = 1
  Length = 225
  Placement = pos=(175,40,-148) rot=(0,0,1;3.14159rad)
  Width = 20
FEATURE [Part::MultiFuse] Fusion015
  Placement = pos=(0,0,0) rot=(0,0,1;3.14159rad)
  Shapes = -> [Box118,Box119,Box120,Box121,Box122,Box123,Box124,Box126,Box125,Box127,Box129,Box128,Box130,Box131,Box132,Box133,Box135,Box134,Box136,Box137,Box138,Box139,Box140,Box149,Box148,Box147,Box145,Box144,Box141,Box142,Box143,Box146]
FEATURE [Part::MultiFuse] Fusion016  label="CompletoConParedes003"
  Shapes = -> [Fusion015,Box150,Box151,Box152,Box153]
FEATURE [Part::Cut] Cut005  label="Parte2"
  Base = -> Fusion016
  Tool = -> Cut004
FEATURE [Part::Box] Box154  label="Cubo154"
  AttacherType = Attacher::AttachEngine3D
  Height = 200
  Length = 300
  Placement = pos=(-197,-27,-241) rot=(0,0,1;0rad)
  Width = 50
FEATURE [Part::Cut] Cut006
  Base = -> Cut002_solid
  Placement = pos=(121,44,3) rot=(0,0,1;0rad)
  Tool = -> Box154
FEATURE [Part::Box] Box155  label="Cubo155"
  AttacherType = Attacher::AttachEngine3D
  Height = 9
  Length = 10
  Placement = pos=(-57,15,-40) rot=(0,0,1;0rad)
  Width = 27
FEATURE [Part::Box] Box156  label="Cubo156"
  AttacherType = Attacher::AttachEngine3D
  Height = 9
  Length = 10
  Placement = pos=(170,15,-40) rot=(0,0,1;0rad)
  Width = 27
FEATURE [Part::Cut] Cut007
  Base = -> Cut006
  Tool = -> Box155
FEATURE [Part::Cut] Cut008
  Base = -> Cut007
  Placement = pos=(0,0,-3) rot=(0,0,1;0rad)
  Tool = -> Box156
FEATURE [Part::MultiFuse] Fusion017
  Shapes = -> [Cut,Cut008]
FEATURE [Part::MultiFuse] Fusion020  label="Parte2Completa"
  Shapes = -> [Cut005,Box039]
FEATURE [Part::Feature] Fusion020_solid  label="Parte2Completa (Solid)"
  shape: bbox 225 x 37 x 170.3 mm, 112 faces (baked)
FEATURE [Part::Cut] Cut009
  Base = -> Fusion017
  Tool = -> Box044
FEATURE [Part::MultiFuse] Fusion021  label="Parte1Completa"
  Shapes = -> [Box041,Box042,Box043,Cut009]
